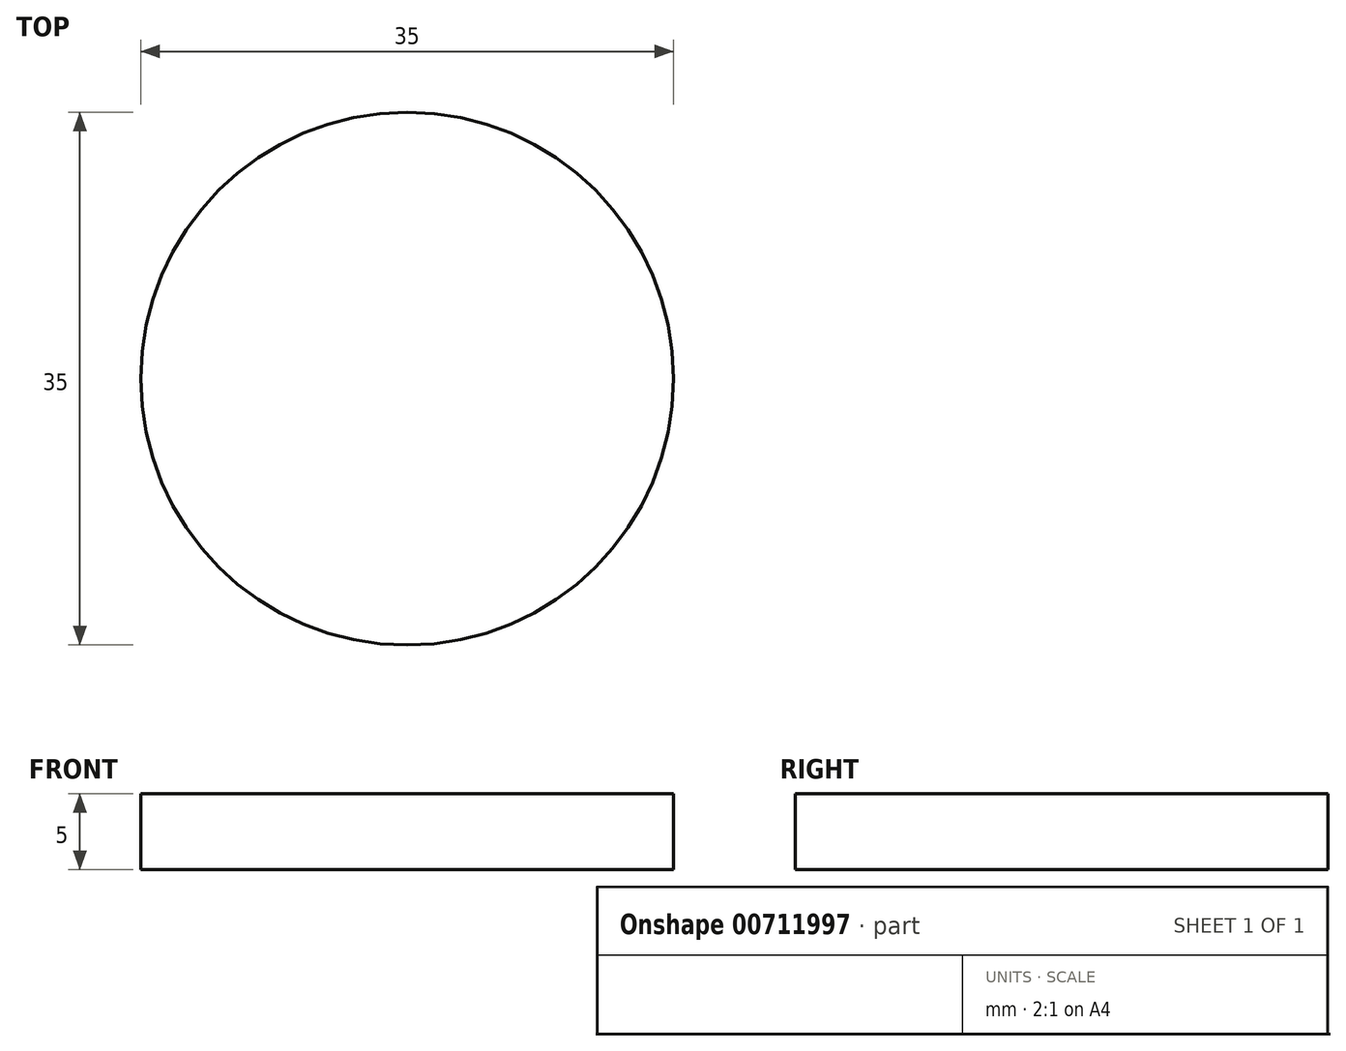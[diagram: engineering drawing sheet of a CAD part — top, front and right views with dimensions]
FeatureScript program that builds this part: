
annotation { "Feature Type Name" : "Feature", "Feature Type Description" : "" }
export const myFeature = defineFeature(function(context is Context, id is Id, definition is map)
    precondition{}
    {
        {
            var Q0;
            Q0=qCreatedBy(makeId("Top.planeOp"),FACE);
            var sketch = newSketch(context, id + "F0", { "sketchPlane" : qUnion([Q0])});
            skCircle(sketch, "E0", {"center": v(0, 0) * mm, "radius": 17.5 * mm});
            skSolve(sketch);
        }
        {
            var Q0;
            Q0=qSketchRegion(id+"F0",true);
            extrude(context, id + "F1", {"entities" : qUnion([Q0]), "depth" : 5 * mm, "offsetDistance" : 25 * mm});
        }
    });
